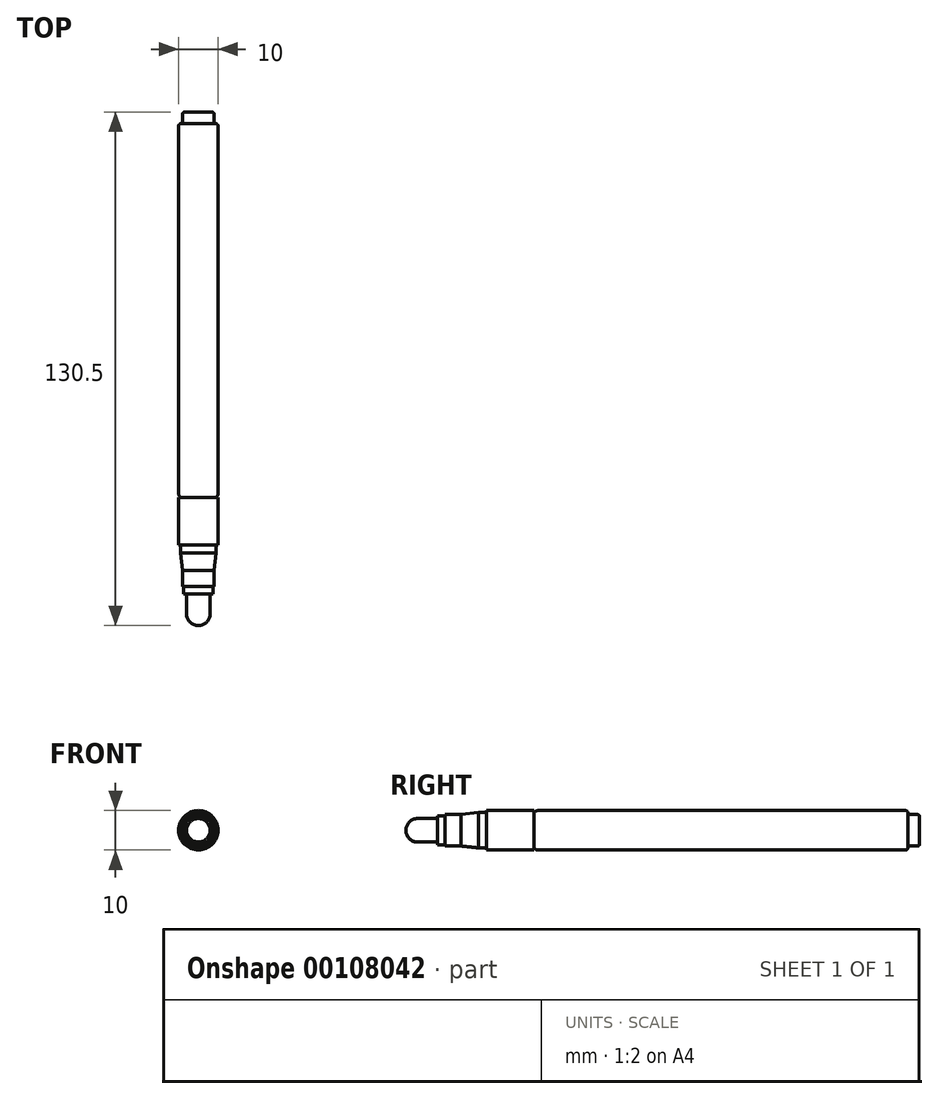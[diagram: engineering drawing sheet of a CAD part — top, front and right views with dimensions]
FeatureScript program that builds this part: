
annotation { "Feature Type Name" : "Feature", "Feature Type Description" : "" }
export const myFeature = defineFeature(function(context is Context, id is Id, definition is map)
    precondition{}
    {
        {
            var Q0;
            Q0=qCreatedBy(makeId("Front.planeOp"),FACE);
            var sketch = newSketch(context, id + "F0", { "sketchPlane" : qUnion([Q0])});
            skCircle(sketch, "E0", {"center": v(0, 0) * mm, "radius": 4 * mm});
            skSolve(sketch);
        }
        {
            var Q0;
            Q0 = qSketchRegion(id + "F0", true);
            extrude(context, id + "F1", {"entities" : qUnion([Q0]), "depth" : 3 * mm});
        }
        {
            var Q0;
            Q0=makeQuery(id+"F1.opExtrude","CAP_FACE",FACE,{"disambiguationData":[OSD([sQuery(id+"F0.wireOp",EDGE,"E0")])],"isStart":false});
            var sketch = newSketch(context, id + "F2", { "sketchPlane" : qUnion([Q0])});
            skCircle(sketch, "E1", {"center": v(0, 0) * mm, "radius": 5 * mm});
            skSolve(sketch);
        }
        {
            var Q0;
            Q0 = qSketchRegion(id + "F2", true);
            extrude(context, id + "F3", {"entities" : qUnion([Q0]), "operationType" : NewBodyOperationType.ADD, "depth" : 95 * mm});
        }
        {
            var Q0;
            Q0=makeQuery(id+"F3.opExtrude","CAP_EDGE",EDGE,{"disambiguationData":[OSD([sQuery(id+"F2.wireOp",EDGE,"E1")])],"isStart":false});
            fillet(context, id + "F4", {"entities" : qUnion([Q0]), "radius" : 1 * mm, "tangentPropagation" : true, "allowEdgeOverflow" : false});
        }
        {
            var Q0;
            Q0=makeQuery(id+"F3.opExtrude","CAP_FACE",FACE,{"disambiguationData":[OSD([sQuery(id+"F2.wireOp",EDGE,"E1")])],"isStart":false});
            var sketch = newSketch(context, id + "F5", { "sketchPlane" : qUnion([Q0])});
            skCircle(sketch, "E2", {"center": v(0, 0) * mm, "radius": 5 * mm});
            skSolve(sketch);
        }
        {
            var Q0;
            Q0 = qSketchRegion(id + "F5", true);
            extrude(context, id + "F6", {"entities" : qUnion([Q0]), "depth" : 12 * mm});
        }
        {
            var Q0;
            Q0=qCreatedBy(makeId("Right.planeOp"),FACE);
            var sketch = newSketch(context, id + "F7", { "sketchPlane" : qUnion([Q0])});
            skLineSegment(sketch, "E3", {"start": v(-110, -4.49) * mm, "end": v(-112, -4.49) * mm});
            skLineSegment(sketch, "E4", {"start": v(-112, -4.49) * mm, "end": v(-116.5, -4) * mm});
            skLineSegment(sketch, "E5", {"start": v(-116.5, -4) * mm, "end": v(-120.5, -4) * mm});
            skLineSegment(sketch, "E6", {"start": v(-120.5, -4) * mm, "end": v(-120.5, -3.7) * mm});
            skLineSegment(sketch, "E7", {"start": v(-120.5, -3.7) * mm, "end": v(-122.5, -3.7) * mm});
            skLineSegment(sketch, "E8", {"start": v(-122.5, -3.7) * mm, "end": v(-122.5, 0) * mm});
            skLineSegment(sketch, "E9", {"start": v(-122.5, 0) * mm, "end": v(-110, 0) * mm});
            skLineSegment(sketch, "E10", {"start": v(-110, 0) * mm, "end": v(-110, -4.49) * mm});
            skSolve(sketch);
        }
        {
            var Q0;
            Q0=makeQuery(id+"F7.imprint","IMPRINT",FACE,{"disambiguationData":[TD([[makeQuery(id+"F7.imprint","IMPRINT",EDGE,{"derivedFrom":sQuery(id+"F7.wireOp",EDGE,"E3")}),-1.0]])]});
            var Q1;
            Q1=sQuery(id+"F7.wireOp",EDGE,"E9");
            revolve(context, id + "F8", {"operationType" : NewBodyOperationType.ADD, "entities" : qUnion([Q0]), "axis" : qUnion([Q1]), "revolveType" : RevolveType.FULL});
        }
        {
            var Q0;
            Q0=makeQuery(id+"F8.opRevolve","SWEPT_FACE",FACE,{"disambiguationData":[OSD([sQuery(id+"F7.wireOp",EDGE,"E8")])]});
            var sketch = newSketch(context, id + "F9", { "sketchPlane" : qUnion([Q0])});
            skCircle(sketch, "E11", {"center": v(0, 0) * mm, "radius": 3 * mm});
            skSolve(sketch);
        }
        {
            var Q0;
            Q0 = qSketchRegion(id + "F9", true);
            extrude(context, id + "F10", {"entities" : qUnion([Q0]), "depth" : 8 * mm});
        }
        {
            var Q0;
            Q0=makeQuery(id+"F10.opExtrude","CAP_EDGE",EDGE,{"disambiguationData":[OSD([sQuery(id+"F9.wireOp",EDGE,"E11")])],"isStart":false});
            fillet(context, id + "F11", {"entities" : qUnion([Q0]), "radius" : 3 * mm, "tangentPropagation" : true, "allowEdgeOverflow" : false});
        }
        {
            var Q0;
            Q0=makeQuery(id+"F3.opExtrude","CAP_EDGE",EDGE,{"disambiguationData":[OSD([sQuery(id+"F2.wireOp",EDGE,"E1")])],"isStart":true});
            var Q1;
            Q1=makeQuery(id+"F1.opExtrude","CAP_EDGE",EDGE,{"disambiguationData":[OSD([sQuery(id+"F0.wireOp",EDGE,"E0")])],"isStart":true});
            fillet(context, id + "F12", {"entities" : qUnion([Q0, Q1]), "radius" : 0.5 * mm, "tangentPropagation" : true, "allowEdgeOverflow" : false});
        }
    });
